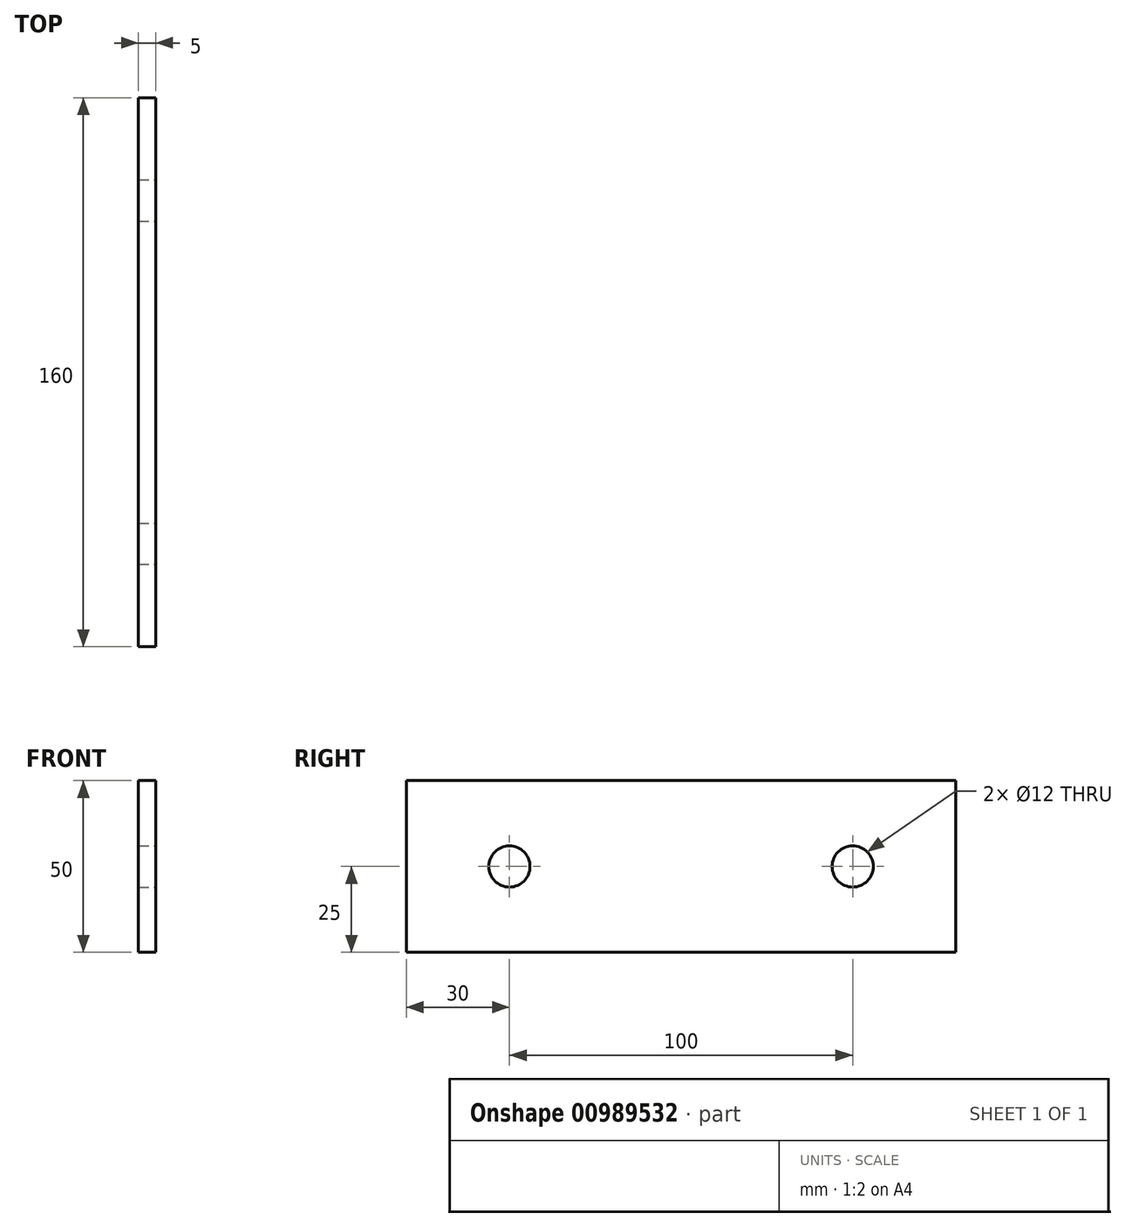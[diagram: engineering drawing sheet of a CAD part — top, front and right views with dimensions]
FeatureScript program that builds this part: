
annotation { "Feature Type Name" : "Feature", "Feature Type Description" : "" }
export const myFeature = defineFeature(function(context is Context, id is Id, definition is map)
    precondition{}
    {
        {
            var Q0;
            Q0=qCreatedBy(makeId("Right.planeOp"),FACE);
            var sketch = newSketch(context, id + "F0", { "sketchPlane" : qUnion([Q0])});
            skLineSegment(sketch, "E0.bottom", {"start": v(-80, 25) * mm, "end": v(80, 25) * mm});
            skLineSegment(sketch, "E0.top", {"start": v(-80, -25) * mm, "end": v(80, -25) * mm});
            skLineSegment(sketch, "E0.left", {"start": v(-80, 25) * mm, "end": v(-80, -25) * mm});
            skLineSegment(sketch, "E0.right", {"start": v(80, 25) * mm, "end": v(80, -25) * mm});
            skPoint(sketch, "E1", {"position": v(-50, 0) * mm});
            skPoint(sketch, "E2", {"position": v(0, 0) * mm});
            skPoint(sketch, "E3", {"position": v(50, 0) * mm});
            skCircle(sketch, "E4", {"center": v(-50, 0) * mm, "radius": 6 * mm});
            skCircle(sketch, "E5", {"center": v(50, 0) * mm, "radius": 6 * mm});
            skSolve(sketch);
        }
        {
            var Q0;
            Q0=makeQuery(id+"F0.imprint","IMPRINT",FACE,{"disambiguationData":[TD([[makeQuery(id+"F0.imprint","IMPRINT",EDGE,{"derivedFrom":sQuery(id+"F0.wireOp",EDGE,"E0.bottom")}),-1.0]])]});
            extrude(context, id + "F1", {"entities" : qUnion([Q0]), "oppositeDirection" : true, "depth" : 5 * mm, "offsetDistance" : 25 * mm});
        }
    });
